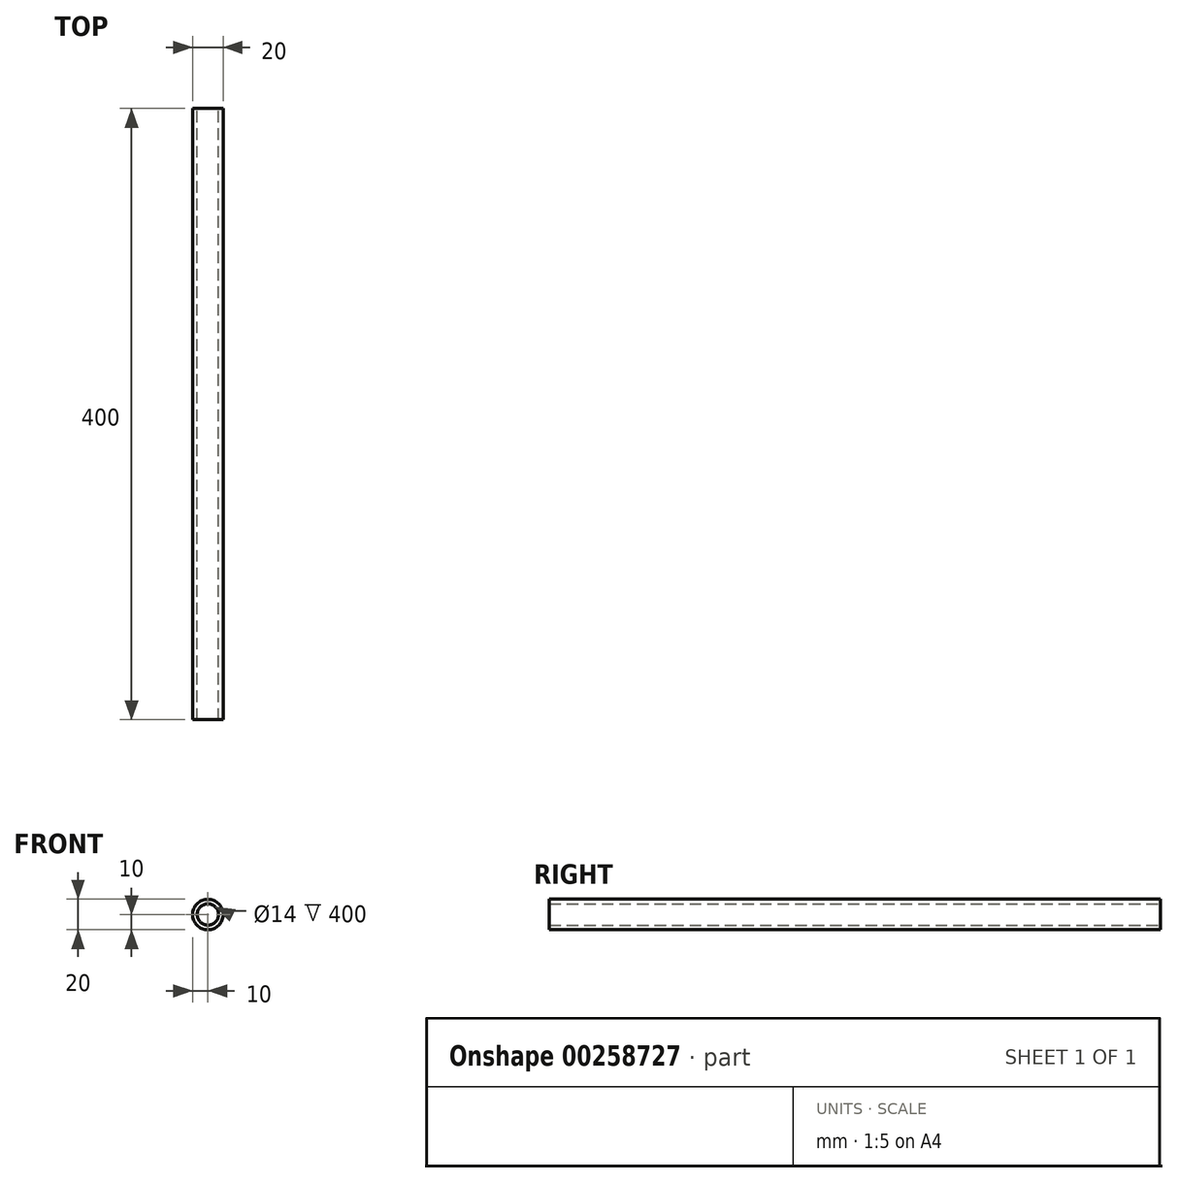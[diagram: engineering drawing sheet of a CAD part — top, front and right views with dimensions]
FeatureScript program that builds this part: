
annotation { "Feature Type Name" : "Feature", "Feature Type Description" : "" }
export const myFeature = defineFeature(function(context is Context, id is Id, definition is map)
    precondition{}
    {
        {
            var Q0;
            Q0=qCreatedBy(makeId("Front.planeOp"),FACE);
            var sketch = newSketch(context, id + "F0", { "sketchPlane" : qUnion([Q0])});
            skCircle(sketch, "E0", {"center": v(0, 0) * mm, "radius": 10 * mm});
            skCircle(sketch, "E1", {"center": v(0, 0) * mm, "radius": 7 * mm});
            skSolve(sketch);
        }
        {
            var Q0;
            Q0=makeQuery(id+"F0.imprint","IMPRINT",FACE,{"disambiguationData":[TD([[makeQuery(id+"F0.imprint","IMPRINT",EDGE,{"derivedFrom":sQuery(id+"F0.wireOp",EDGE,"E0")}),1.0]])]});
            extrude(context, id + "F1", {"entities" : qUnion([Q0]), "depth" : 400 * mm});
        }
    });
